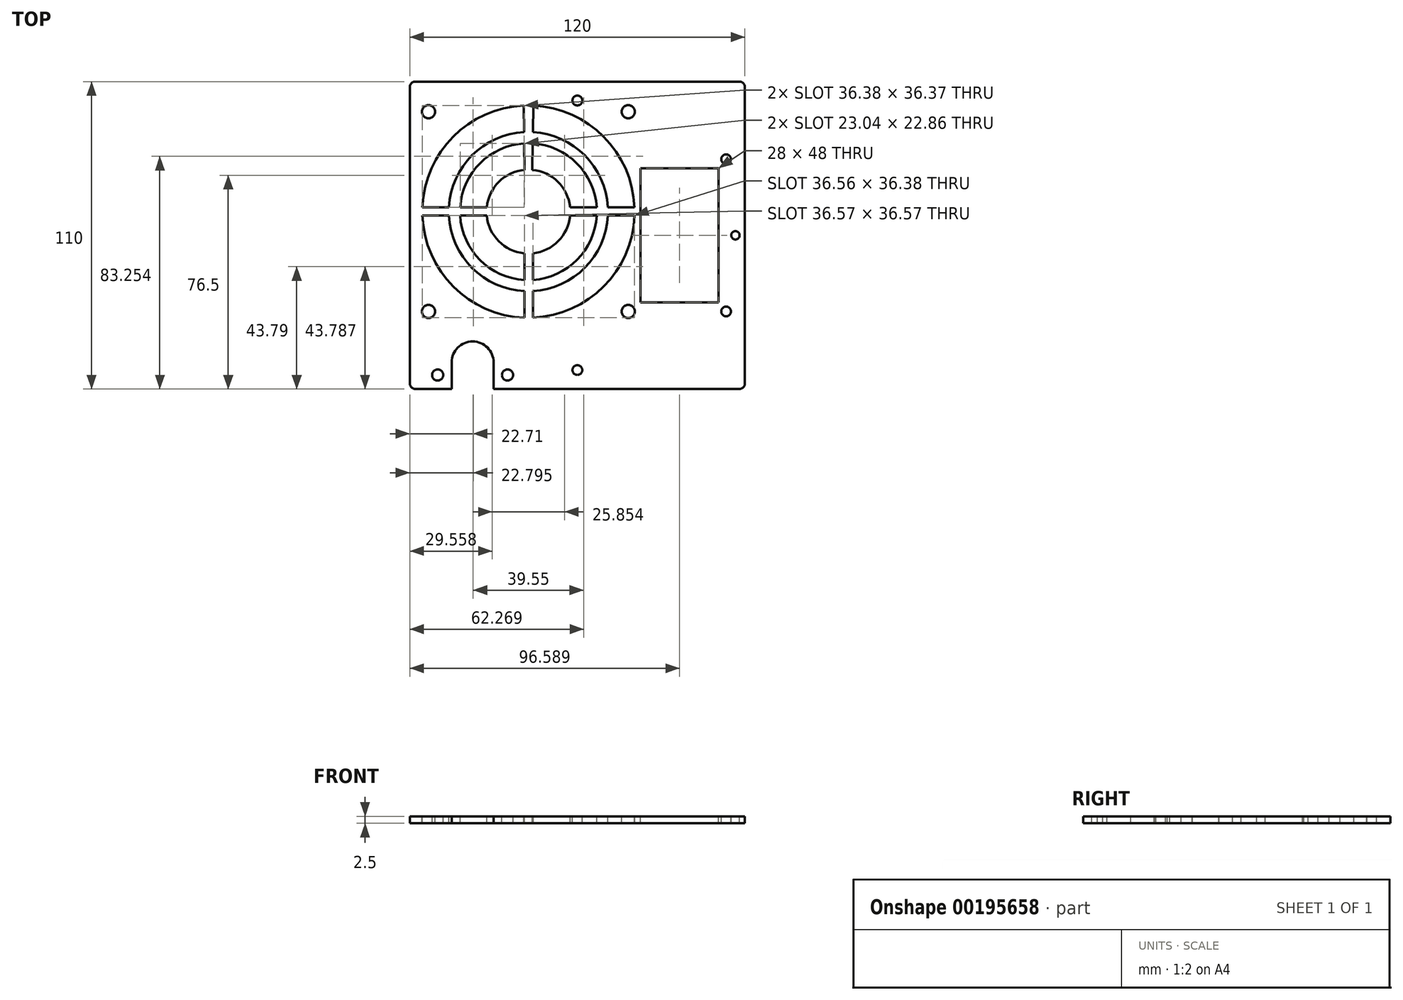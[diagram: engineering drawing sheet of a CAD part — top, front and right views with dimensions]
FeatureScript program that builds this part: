
annotation { "Feature Type Name" : "Feature", "Feature Type Description" : "" }
export const myFeature = defineFeature(function(context is Context, id is Id, definition is map)
    precondition{}
    {
        {
            var Q0;
            Q0=qCreatedBy(makeId("Top.planeOp"),FACE);
            var sketch = newSketch(context, id + "F0", { "sketchPlane" : qUnion([Q0])});
            skLineSegment(sketch, "E0.bottom", {"start": v(-58, 55) * mm, "end": v(58, 55) * mm});
            skLineSegment(sketch, "E0.top", {"start": v(-58, -55) * mm, "end": v(58, -55) * mm});
            skLineSegment(sketch, "E0.left", {"start": v(-60, 53) * mm, "end": v(-60, -53) * mm});
            skLineSegment(sketch, "E0.right", {"start": v(60, 53) * mm, "end": v(60, -53) * mm});
            skPoint(sketch, "E1", {"position": v(60, 0) * mm});
            skPoint(sketch, "E2", {"position": v(0, -55) * mm});
            skPoint(sketch, "E3.visualSharp", {"position": v(-60, 55) * mm});
            skArc(sketch, "E3.filletArc", {"start": v(-58, 55) * mm, "mid": v(-59.41, 54.41) * mm, "end": v(-60, 53) * mm});
            skPoint(sketch, "E4.visualSharp", {"position": v(60, 55) * mm});
            skArc(sketch, "E4.filletArc", {"start": v(60, 53) * mm, "mid": v(59.41, 54.41) * mm, "end": v(58, 55) * mm});
            skPoint(sketch, "E5.visualSharp", {"position": v(60, -55) * mm});
            skArc(sketch, "E5.filletArc", {"start": v(58, -55) * mm, "mid": v(59.41, -54.41) * mm, "end": v(60, -53) * mm});
            skPoint(sketch, "E6.visualSharp", {"position": v(-60, -55) * mm});
            skArc(sketch, "E6.filletArc", {"start": v(-60, -53) * mm, "mid": v(-59.41, -54.41) * mm, "end": v(-58, -55) * mm});
            skSolve(sketch);
        }
        {
            var Q0;
            Q0=makeQuery(id+"F0.imprint","IMPRINT",FACE,{"disambiguationData":[TD([[makeQuery(id+"F0.imprint","IMPRINT",EDGE,{"derivedFrom":sQuery(id+"F0.wireOp",EDGE,"E0.bottom")}),-1.0]])]});
            extrude(context, id + "F1", {"entities" : qUnion([Q0]), "depth" : 2.5 * mm});
        }
        {
            var Q0;
            Q0=makeQuery(id+"F1.opExtrude","CAP_FACE",FACE,{"disambiguationData":[OSD([sQuery(id+"F0.wireOp",EDGE,"E0.bottom"),sQuery(id+"F0.wireOp",EDGE,"E0.top"),sQuery(id+"F0.wireOp",EDGE,"E0.left"),sQuery(id+"F0.wireOp",EDGE,"E0.right"),sQuery(id+"F0.wireOp",EDGE,"E3.filletArc"),sQuery(id+"F0.wireOp",EDGE,"E4.filletArc"),sQuery(id+"F0.wireOp",EDGE,"E5.filletArc"),sQuery(id+"F0.wireOp",EDGE,"E6.filletArc")])],"isStart":false});
            var sketch = newSketch(context, id + "F2", { "sketchPlane" : qUnion([Q0])});
            skCircle(sketch, "E7.MirrorC", {"center": v(53.25, 27.25) * mm, "radius": 1.75 * mm});
            skCircle(sketch, "E8", {"center": v(0, 48.25) * mm, "radius": 1.75 * mm});
            skCircle(sketch, "E9.MirrorC", {"center": v(0, -48.25) * mm, "radius": 1.75 * mm});
            skCircle(sketch, "E10.MirrorC", {"center": v(53.25, -27.25) * mm, "radius": 1.75 * mm});
            skCircle(sketch, "E11.MirrorC", {"center": v(-53.25, -27.25) * mm, "radius": 1.75 * mm});
            skSolve(sketch);
        }
        {
            var Q0;
            Q0 = qSketchRegion(id + "F2", true);
            var Q1;
            Q1=makeQuery(id+"F1.opExtrude","CAP_FACE",FACE,{"disambiguationData":[OSD([sQuery(id+"F0.wireOp",EDGE,"E0.bottom"),sQuery(id+"F0.wireOp",EDGE,"E0.top"),sQuery(id+"F0.wireOp",EDGE,"E0.left"),sQuery(id+"F0.wireOp",EDGE,"E0.right"),sQuery(id+"F0.wireOp",EDGE,"E3.filletArc"),sQuery(id+"F0.wireOp",EDGE,"E4.filletArc"),sQuery(id+"F0.wireOp",EDGE,"E5.filletArc"),sQuery(id+"F0.wireOp",EDGE,"E6.filletArc")])],"isStart":true});
            extrude(context, id + "F3", {"entities" : qUnion([Q0]), "operationType" : NewBodyOperationType.REMOVE, "endBound" : BoundingType.UP_TO_SURFACE, "oppositeDirection" : true, "endBoundEntityFace" : qUnion([Q1]), "depth" : 25 * mm});
        }
        {
            var Q0;
            Q0=makeQuery(id+"F1.opExtrude","CAP_FACE",FACE,{"disambiguationData":[OSD([sQuery(id+"F0.wireOp",EDGE,"E0.bottom"),sQuery(id+"F0.wireOp",EDGE,"E0.top"),sQuery(id+"F0.wireOp",EDGE,"E0.left"),sQuery(id+"F0.wireOp",EDGE,"E0.right"),sQuery(id+"F0.wireOp",EDGE,"E3.filletArc"),sQuery(id+"F0.wireOp",EDGE,"E4.filletArc"),sQuery(id+"F0.wireOp",EDGE,"E5.filletArc"),sQuery(id+"F0.wireOp",EDGE,"E6.filletArc")])],"isStart":false});
            var sketch = newSketch(context, id + "F4", { "sketchPlane" : qUnion([Q0])});
            skLineSegment(sketch, "E12.bottom", {"start": v(-45, -55) * mm, "end": v(-30, -55) * mm});
            skLineSegment(sketch, "E12.left", {"start": v(-45, -55) * mm, "end": v(-45, -45.5) * mm});
            skLineSegment(sketch, "E12.right", {"start": v(-30, -55) * mm, "end": v(-30, -45.5) * mm});
            skArc(sketch, "E13", {"start": v(-45, -45.5) * mm, "mid": v(-37.5, -38) * mm, "end": v(-30, -45.5) * mm});
            skLineSegment(sketch, "E14.bottom", {"start": v(-53.27, 44.23) * mm, "end": v(18.23, 44.23) * mm, "construction": true});
            skLineSegment(sketch, "E14.top", {"start": v(-53.27, -27.27) * mm, "end": v(18.23, -27.27) * mm, "construction": true});
            skLineSegment(sketch, "E14.left", {"start": v(-53.27, 44.23) * mm, "end": v(-53.27, -27.27) * mm, "construction": true});
            skLineSegment(sketch, "E14.right", {"start": v(18.23, 44.23) * mm, "end": v(18.23, -27.27) * mm, "construction": true});
            skCircle(sketch, "E15", {"center": v(-53.27, 44.23) * mm, "radius": 2.35 * mm});
            skCircle(sketch, "E16", {"center": v(18.23, 44.23) * mm, "radius": 2.35 * mm});
            skCircle(sketch, "E17", {"center": v(-53.27, -27.27) * mm, "radius": 2.35 * mm});
            skCircle(sketch, "E18", {"center": v(18.23, -27.27) * mm, "radius": 2.35 * mm});
            skPoint(sketch, "E19", {"position": v(-53.27, 8.48) * mm});
            skPoint(sketch, "E20", {"position": v(-17.52, -27.27) * mm});
            skLineSegment(sketch, "E21", {"start": v(-53.27, 8.48) * mm, "end": v(18.23, 8.48) * mm, "construction": true});
            skLineSegment(sketch, "E22", {"start": v(-17.52, -27.27) * mm, "end": v(-17.52, 44.23) * mm, "construction": true});
            skArc(sketch, "E23.0", {"start": v(-32.45, 7.07) * mm, "mid": v(-28.12, -2.13) * mm, "end": v(-18.92, -6.46) * mm});
            skArc(sketch, "E24.0", {"start": v(-41.97, 7.07) * mm, "mid": v(-34.84, -8.85) * mm, "end": v(-18.92, -15.98) * mm});
            skArc(sketch, "E25.0", {"start": v(-45.98, 7.07) * mm, "mid": v(-37.67, -11.68) * mm, "end": v(-18.92, -19.99) * mm});
            skArc(sketch, "E26.0", {"start": v(-55.49, 7.07) * mm, "mid": v(-44.39, -18.4) * mm, "end": v(-18.92, -29.5) * mm});
            skLineSegment(sketch, "E27.bottom", {"start": v(-55.48, 10.07) * mm, "end": v(-45.97, 10.07) * mm});
            skLineSegment(sketch, "E27.top", {"start": v(-55.49, 7.07) * mm, "end": v(-45.98, 7.07) * mm});
            skLineSegment(sketch, "E28.left", {"start": v(-15.92, -29.49) * mm, "end": v(-15.92, -19.98) * mm});
            skLineSegment(sketch, "E28.right", {"start": v(-18.92, -29.5) * mm, "end": v(-18.92, -19.99) * mm});
            skArc(sketch, "E29.trimOffspring", {"start": v(-2.6, 10.07) * mm, "mid": v(-6.98, 19.15) * mm, "end": v(-16.1, 23.41) * mm});
            skArc(sketch, "E30.trimOffspring", {"start": v(6.93, 10.07) * mm, "mid": v(-0.21, 25.82) * mm, "end": v(-15.98, 32.93) * mm});
            skArc(sketch, "E31.trimOffspring", {"start": v(10.94, 10.07) * mm, "mid": v(2.63, 28.63) * mm, "end": v(-15.93, 36.93) * mm});
            skArc(sketch, "E32.trimOffspring", {"start": v(20.45, 10.07) * mm, "mid": v(9.4, 35.3) * mm, "end": v(-15.8, 46.44) * mm});
            skArc(sketch, "E33.trimOffspring", {"start": v(-15.92, -6.44) * mm, "mid": v(-6.84, -2.06) * mm, "end": v(-2.58, 7.07) * mm});
            skArc(sketch, "E34.trimOffspring", {"start": v(-15.92, -15.97) * mm, "mid": v(-0.12, -8.78) * mm, "end": v(6.94, 7.07) * mm});
            skArc(sketch, "E35.trimOffspring", {"start": v(-15.92, -19.98) * mm, "mid": v(2.7, -11.6) * mm, "end": v(10.95, 7.07) * mm});
            skArc(sketch, "E36.trimOffspring", {"start": v(-15.92, -29.49) * mm, "mid": v(9.42, -18.33) * mm, "end": v(20.46, 7.07) * mm});
            skArc(sketch, "E37.trimOffspring", {"start": v(-19.22, 46.44) * mm, "mid": v(-44.43, 35.3) * mm, "end": v(-55.48, 10.07) * mm});
            skArc(sketch, "E38.trimOffspring", {"start": v(-19.1, 36.93) * mm, "mid": v(-37.66, 28.63) * mm, "end": v(-45.97, 10.07) * mm});
            skArc(sketch, "E39.trimOffspring", {"start": v(-19.05, 32.93) * mm, "mid": v(-34.82, 25.82) * mm, "end": v(-41.96, 10.07) * mm});
            skArc(sketch, "E40.trimOffspring", {"start": v(-18.92, 23.41) * mm, "mid": v(-28.05, 19.15) * mm, "end": v(-32.43, 10.07) * mm});
            skLineSegment(sketch, "E41.trimOffspring", {"start": v(-18.92, 23.41) * mm, "end": v(-19.05, 32.93) * mm});
            skLineSegment(sketch, "E42.trimOffspring", {"start": v(-16.1, 23.41) * mm, "end": v(-15.98, 32.93) * mm});
            skLineSegment(sketch, "E43.trimOffspring", {"start": v(-2.6, 10.07) * mm, "end": v(6.93, 10.07) * mm});
            skLineSegment(sketch, "E44.trimOffspring", {"start": v(-2.58, 7.07) * mm, "end": v(6.94, 7.07) * mm});
            skLineSegment(sketch, "E45.trimOffspring", {"start": v(-18.92, -15.98) * mm, "end": v(-18.92, -6.46) * mm});
            skLineSegment(sketch, "E46.trimOffspring", {"start": v(-15.92, -15.97) * mm, "end": v(-15.92, -6.44) * mm});
            skLineSegment(sketch, "E47.trimOffspring", {"start": v(-41.97, 7.07) * mm, "end": v(-32.45, 7.07) * mm});
            skLineSegment(sketch, "E48.trimOffspring", {"start": v(-41.96, 10.07) * mm, "end": v(-32.43, 10.07) * mm});
            skLineSegment(sketch, "E49.trimOffspring", {"start": v(10.95, 7.07) * mm, "end": v(20.46, 7.07) * mm});
            skLineSegment(sketch, "E50.trimOffspring", {"start": v(10.94, 10.07) * mm, "end": v(20.45, 10.07) * mm});
            skLineSegment(sketch, "E51.trimOffspring", {"start": v(-15.93, 36.93) * mm, "end": v(-15.8, 46.44) * mm});
            skLineSegment(sketch, "E52.trimOffspring", {"start": v(-19.1, 36.93) * mm, "end": v(-19.22, 46.44) * mm});
            skPoint(sketch, "E53", {"position": v(18.23, 8.48) * mm});
            skCircle(sketch, "E54", {"center": v(-50, -50) * mm, "radius": 2 * mm});
            skCircle(sketch, "E55", {"center": v(-25, -50) * mm, "radius": 2 * mm});
            skSolve(sketch);
        }
        {
            var Q0;
            Q0 = qSketchRegion(id + "F4", true);
            var Q1;
            Q1=makeQuery(id+"F1.opExtrude","CAP_FACE",FACE,{"disambiguationData":[OSD([sQuery(id+"F0.wireOp",EDGE,"E0.bottom"),sQuery(id+"F0.wireOp",EDGE,"E0.top"),sQuery(id+"F0.wireOp",EDGE,"E0.left"),sQuery(id+"F0.wireOp",EDGE,"E0.right"),sQuery(id+"F0.wireOp",EDGE,"E3.filletArc"),sQuery(id+"F0.wireOp",EDGE,"E4.filletArc"),sQuery(id+"F0.wireOp",EDGE,"E5.filletArc"),sQuery(id+"F0.wireOp",EDGE,"E6.filletArc")])],"isStart":true});
            extrude(context, id + "F5", {"entities" : qUnion([Q0]), "operationType" : NewBodyOperationType.REMOVE, "endBound" : BoundingType.UP_TO_SURFACE, "oppositeDirection" : true, "endBoundEntityFace" : qUnion([Q1]), "depth" : 25 * mm});
        }
        {
            var Q0;
            Q0=makeQuery(id+"F1.opExtrude","CAP_FACE",FACE,{"disambiguationData":[OSD([sQuery(id+"F0.wireOp",EDGE,"E0.bottom"),sQuery(id+"F0.wireOp",EDGE,"E0.top"),sQuery(id+"F0.wireOp",EDGE,"E0.left"),sQuery(id+"F0.wireOp",EDGE,"E0.right"),sQuery(id+"F0.wireOp",EDGE,"E3.filletArc"),sQuery(id+"F0.wireOp",EDGE,"E4.filletArc"),sQuery(id+"F0.wireOp",EDGE,"E5.filletArc"),sQuery(id+"F0.wireOp",EDGE,"E6.filletArc")])],"isStart":false});
            var sketch = newSketch(context, id + "F6", { "sketchPlane" : qUnion([Q0])});
            skPoint(sketch, "E56", {"position": v(31, -50) * mm});
            skPoint(sketch, "E57", {"position": v(31, -22) * mm});
            skLineSegment(sketch, "E58.bottom", {"start": v(22.59, 24) * mm, "end": v(50.59, 24) * mm});
            skLineSegment(sketch, "E58.top", {"start": v(22.59, -24) * mm, "end": v(50.59, -24) * mm});
            skLineSegment(sketch, "E58.left", {"start": v(22.59, 24) * mm, "end": v(22.59, -24) * mm});
            skLineSegment(sketch, "E58.right", {"start": v(50.59, 24) * mm, "end": v(50.59, -24) * mm});
            skCircle(sketch, "E59", {"center": v(56.59, 0) * mm, "radius": 1.5 * mm});
            skPoint(sketch, "E60", {"position": v(50.59, 0) * mm});
            skSolve(sketch);
        }
        {
            var Q0;
            Q0 = qSketchRegion(id + "F6", true);
            var Q1;
            Q1=makeQuery(id+"F1.opExtrude","CAP_FACE",FACE,{"disambiguationData":[OSD([sQuery(id+"F0.wireOp",EDGE,"E0.bottom"),sQuery(id+"F0.wireOp",EDGE,"E0.top"),sQuery(id+"F0.wireOp",EDGE,"E0.left"),sQuery(id+"F0.wireOp",EDGE,"E0.right"),sQuery(id+"F0.wireOp",EDGE,"E3.filletArc"),sQuery(id+"F0.wireOp",EDGE,"E4.filletArc"),sQuery(id+"F0.wireOp",EDGE,"E5.filletArc"),sQuery(id+"F0.wireOp",EDGE,"E6.filletArc")])],"isStart":true});
            extrude(context, id + "F7", {"entities" : qUnion([Q0]), "operationType" : NewBodyOperationType.REMOVE, "endBound" : BoundingType.UP_TO_SURFACE, "oppositeDirection" : true, "endBoundEntityFace" : qUnion([Q1]), "depth" : 25 * mm});
        }
    });
